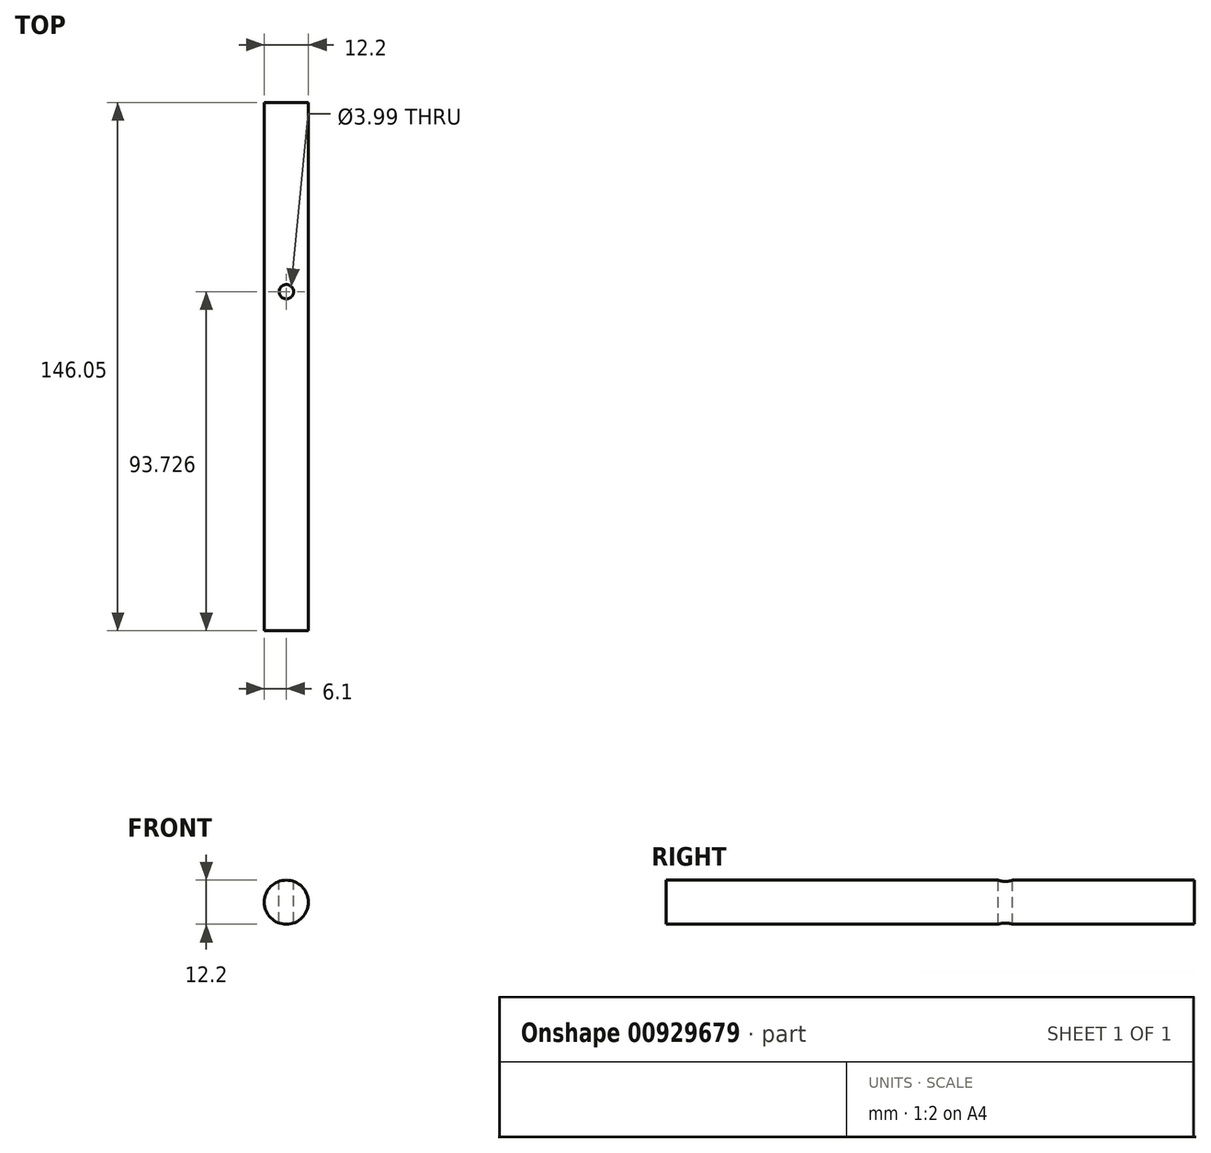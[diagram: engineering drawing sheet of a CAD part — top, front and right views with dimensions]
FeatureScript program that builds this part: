
annotation { "Feature Type Name" : "Feature", "Feature Type Description" : "" }
export const myFeature = defineFeature(function(context is Context, id is Id, definition is map)
    precondition{}
    {
        {
            var Q0;
            Q0=qCreatedBy(makeId("Front.planeOp"),FACE);
            var sketch = newSketch(context, id + "F0", { "sketchPlane" : qUnion([Q0])});
            skCircle(sketch, "E0", {"center": v(0, 0) * mm, "radius": 6.1 * mm});
            skSolve(sketch);
        }
        {
            var Q0;
            Q0=makeQuery(id+"F0.imprint","IMPRINT",FACE,{"disambiguationData":[TD([[makeQuery(id+"F0.imprint","IMPRINT",EDGE,{"derivedFrom":sQuery(id+"F0.wireOp",EDGE,"E0")}),1.0]])]});
            extrude(context, id + "F1", {"entities" : qUnion([Q0]), "depth" : 146.05 * mm, "offsetDistance" : 25.4 * mm});
        }
        {
            var Q0;
            Q0=qCreatedBy(makeId("Top.planeOp"),FACE);
            var sketch = newSketch(context, id + "F2", { "sketchPlane" : qUnion([Q0])});
            skCircle(sketch, "E1", {"center": v(0, -52.32) * mm, "radius": 2 * mm});
            skSolve(sketch);
        }
        {
            var Q0;
            Q0=qSketchRegion(id+"F2",true);
            extrude(context, id + "F3", {"entities" : qUnion([Q0]), "operationType" : NewBodyOperationType.REMOVE, "endBound" : BoundingType.SYMMETRIC, "oppositeDirection" : true, "depth" : 25.4 * mm, "offsetDistance" : 25.4 * mm});
        }
    });
